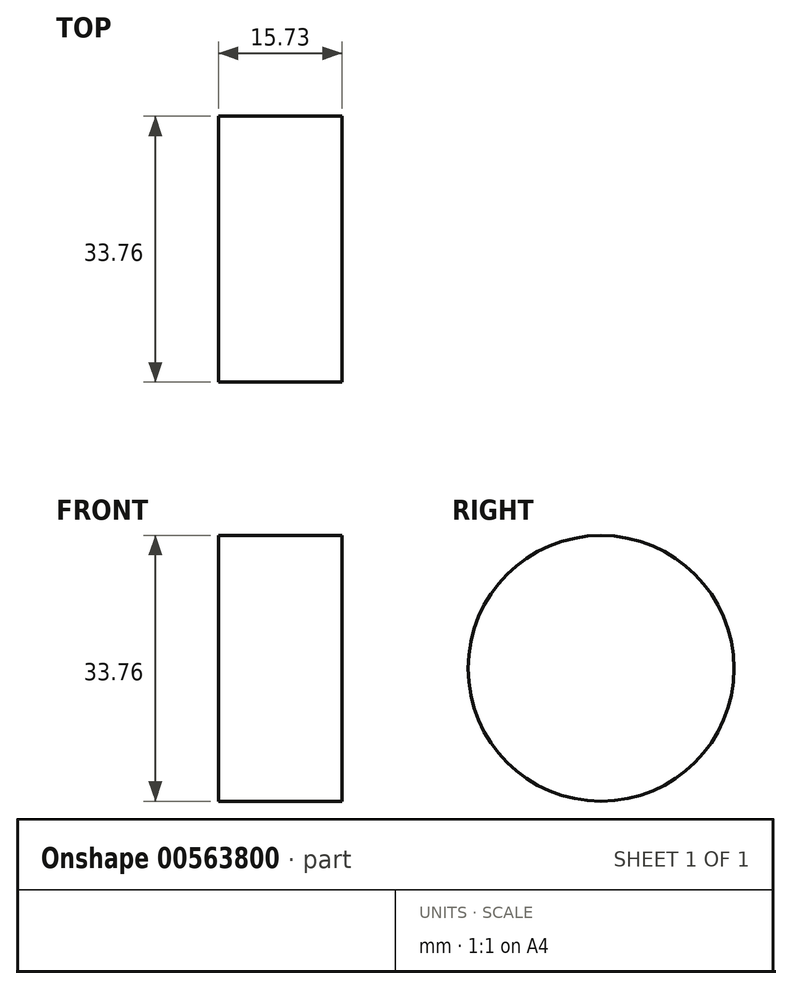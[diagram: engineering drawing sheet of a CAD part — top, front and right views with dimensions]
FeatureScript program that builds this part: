
annotation { "Feature Type Name" : "Feature", "Feature Type Description" : "" }
export const myFeature = defineFeature(function(context is Context, id is Id, definition is map)
    precondition{}
    {
        {
            var Q0;
            Q0=qCreatedBy(makeId("Right.planeOp"),FACE);
            var sketch = newSketch(context, id + "F0", { "sketchPlane" : qUnion([Q0])});
            skCircle(sketch, "E0", {"center": v(-54.13, -32.08) * mm, "radius": 16.88 * mm});
            skSolve(sketch);
        }
        {
            var Q0;
            Q0=makeQuery(id+"F0.imprint","IMPRINT",FACE,{"disambiguationData":[TD([[makeQuery(id+"F0.imprint","IMPRINT",EDGE,{"derivedFrom":sQuery(id+"F0.wireOp",EDGE,"E0")}),1.0]])]});
            extrude(context, id + "F1", {"entities" : qUnion([Q0]), "depth" : 15.73 * mm, "offsetDistance" : 25.4 * mm});
        }
    });
